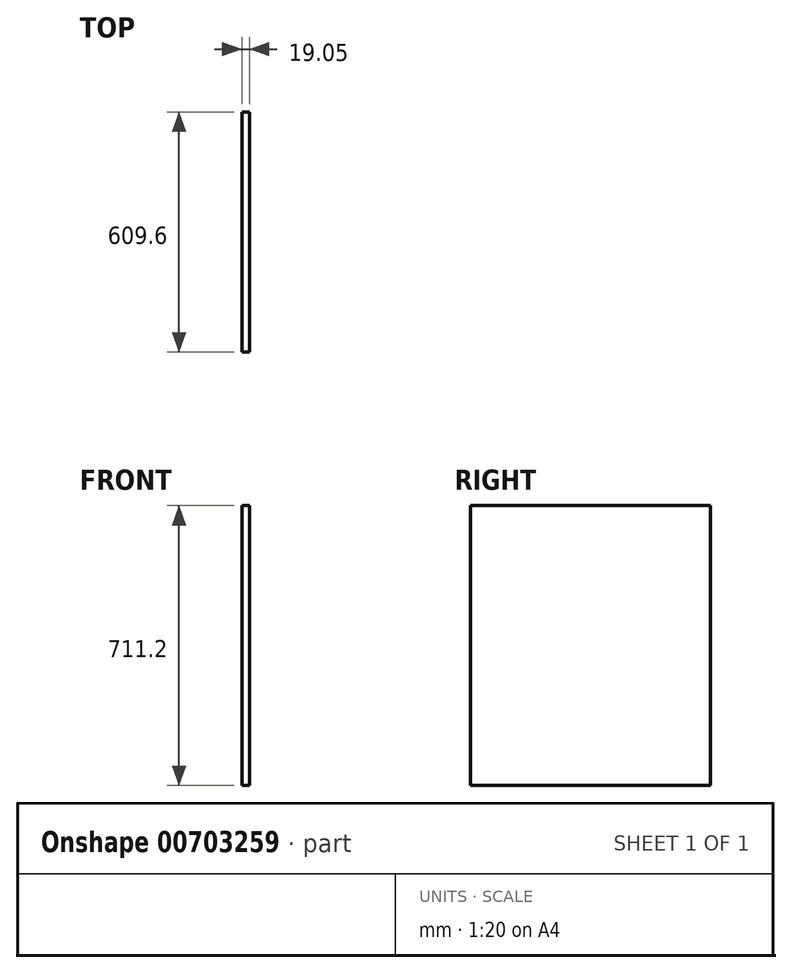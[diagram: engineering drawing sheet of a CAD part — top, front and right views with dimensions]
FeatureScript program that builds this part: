
annotation { "Feature Type Name" : "Feature", "Feature Type Description" : "" }
export const myFeature = defineFeature(function(context is Context, id is Id, definition is map)
    precondition{}
    {
        {
            var Q0;
            Q0=qCreatedBy(makeId("Right.planeOp"),FACE);
            var sketch = newSketch(context, id + "F0", { "sketchPlane" : qUnion([Q0])});
            skLineSegment(sketch, "E0.bottom", {"start": v(304.8, 355.6) * mm, "end": v(-304.8, 355.6) * mm});
            skLineSegment(sketch, "E0.top", {"start": v(304.8, -355.6) * mm, "end": v(-304.8, -355.6) * mm});
            skLineSegment(sketch, "E0.left", {"start": v(304.8, 355.6) * mm, "end": v(304.8, -355.6) * mm});
            skLineSegment(sketch, "E0.right", {"start": v(-304.8, 355.6) * mm, "end": v(-304.8, -355.6) * mm});
            skPoint(sketch, "E0.middle", {"position": v(0, 0) * mm});
            skSolve(sketch);
        }
        {
            var Q0;
            Q0=makeQuery(id+"F0.imprint","IMPRINT",FACE,{"disambiguationData":[TD([[makeQuery(id+"F0.imprint","IMPRINT",EDGE,{"derivedFrom":sQuery(id+"F0.wireOp",EDGE,"E0.bottom")}),1.0]])]});
            extrude(context, id + "F1", {"entities" : qUnion([Q0]), "depth" : 19.05 * mm, "offsetDistance" : 25.4 * mm});
        }
    });
